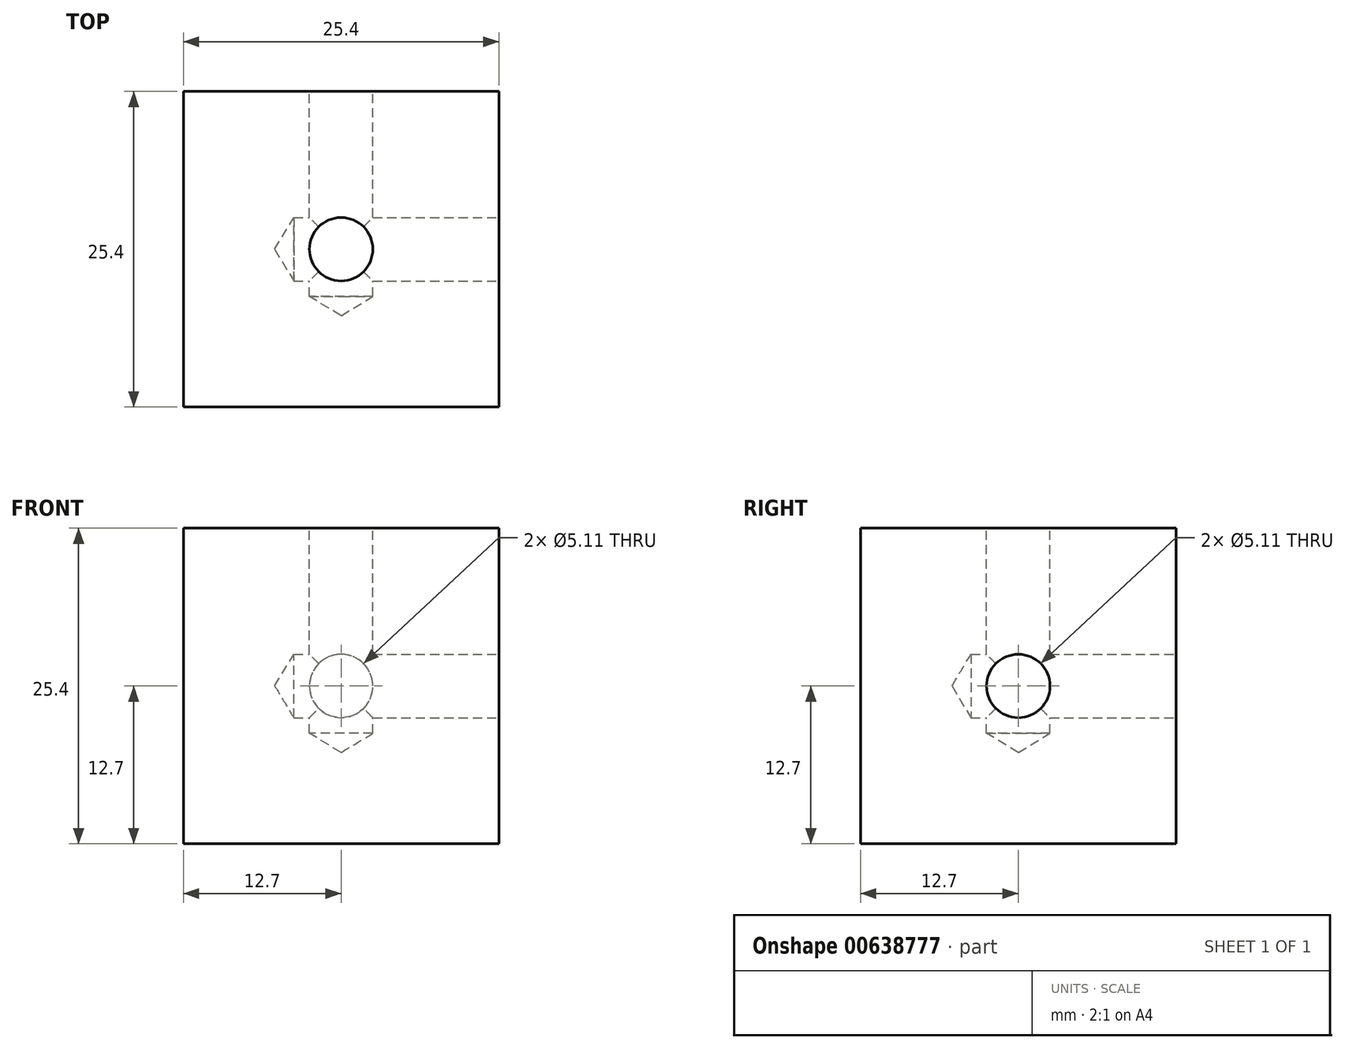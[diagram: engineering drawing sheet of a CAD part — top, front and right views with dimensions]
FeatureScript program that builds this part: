
annotation { "Feature Type Name" : "Feature", "Feature Type Description" : "" }
export const myFeature = defineFeature(function(context is Context, id is Id, definition is map)
    precondition{}
    {
        {
            var Q0;
            Q0=qCreatedBy(makeId("Top.planeOp"),FACE);
            var sketch = newSketch(context, id + "F0", { "sketchPlane" : qUnion([Q0])});
            skLineSegment(sketch, "E0.bottom", {"start": v(-12.7, -12.7) * mm, "end": v(12.7, -12.7) * mm});
            skLineSegment(sketch, "E0.top", {"start": v(-12.7, 12.7) * mm, "end": v(12.7, 12.7) * mm});
            skLineSegment(sketch, "E0.left", {"start": v(-12.7, -12.7) * mm, "end": v(-12.7, 12.7) * mm});
            skLineSegment(sketch, "E0.right", {"start": v(12.7, -12.7) * mm, "end": v(12.7, 12.7) * mm});
            skPoint(sketch, "E0.middle", {"position": v(0, 0) * mm});
            skSolve(sketch);
        }
        {
            var Q0;
            Q0 = qSketchRegion(id + "F0", true);
            extrude(context, id + "F1", {"entities" : qUnion([Q0]), "depth" : 25.4 * mm, "offsetDistance" : 25.4 * mm});
        }
        {
            var Q0;
            Q0=makeQuery(id+"F1.opExtrude","CAP_FACE",FACE,{"disambiguationData":[OSD([sQuery(id+"F0.wireOp",EDGE,"E0.bottom"),sQuery(id+"F0.wireOp",EDGE,"E0.top"),sQuery(id+"F0.wireOp",EDGE,"E0.left"),sQuery(id+"F0.wireOp",EDGE,"E0.right")])],"isStart":false});
            var sketch = newSketch(context, id + "F2", { "sketchPlane" : qUnion([Q0])});
            skPoint(sketch, "E1", {"position": v(0, 0) * mm});
            skSolve(sketch);
        }
        {
            var Q0;
            Q0=makeQuery(id+"F1.opExtrude","SWEPT_FACE",FACE,{"disambiguationData":[OSD([sQuery(id+"F0.wireOp",EDGE,"E0.right")])]});
            var sketch = newSketch(context, id + "F3", { "sketchPlane" : qUnion([Q0])});
            skPoint(sketch, "E2", {"position": v(0, 12.7) * mm});
            skSolve(sketch);
        }
        {
            var Q0;
            Q0=makeQuery(id+"F1.opExtrude","SWEPT_FACE",FACE,{"disambiguationData":[OSD([sQuery(id+"F0.wireOp",EDGE,"E0.top")])]});
            var sketch = newSketch(context, id + "F4", { "sketchPlane" : qUnion([Q0])});
            skPoint(sketch, "E3", {"position": v(0, 12.7) * mm});
            skSolve(sketch);
        }
        {
            var Q0;
            Q0=sQuery(id+"F2.wireOp",VERTEX,"E1");
            var Q1;
            Q1=sQuery(id+"F3.wireOp",VERTEX,"E2");
            var Q2;
            Q2=sQuery(id+"F4.wireOp",VERTEX,"E3");
            var Q3;
            Q3=makeQuery(id+"F1.opExtrude","SWEPT_BODY",BODY,{"disambiguationData":[OSD([sQuery(id+"F0.wireOp",EDGE,"E0.bottom"),sQuery(id+"F0.wireOp",EDGE,"E0.top"),sQuery(id+"F0.wireOp",EDGE,"E0.left"),sQuery(id+"F0.wireOp",EDGE,"E0.right")])]});
            hole(context, id + "F5", {"style" : HoleStyle.SIMPLE, "endStyle" : HoleEndStyle.BLIND, "standardTappedOrClearance" : lookupTablePath({ "standard" : "ANSI", "engagement" : "75%", "pitch" : "20 tpi", "size" : "1/4", "type" : "Tapped" }), "standardBlindInLast" : lookupTablePath({ "standard" : "ANSI", "engagement" : "75%", "pitch" : "20 tpi", "size" : "1/4", "type" : "Tapped" }), "holeDiameter" : 5.1 * mm, "majorDiameter" : 6.35 * mm, "showTappedDepth" : true, "holeDepth" : 16.51 * mm, "tappedDepth" : 12.7 * mm, "tapClearance" : 3, "locations" : qUnion([Q0, Q1, Q2]), "scope" : qUnion([Q3])});
        }
    });
